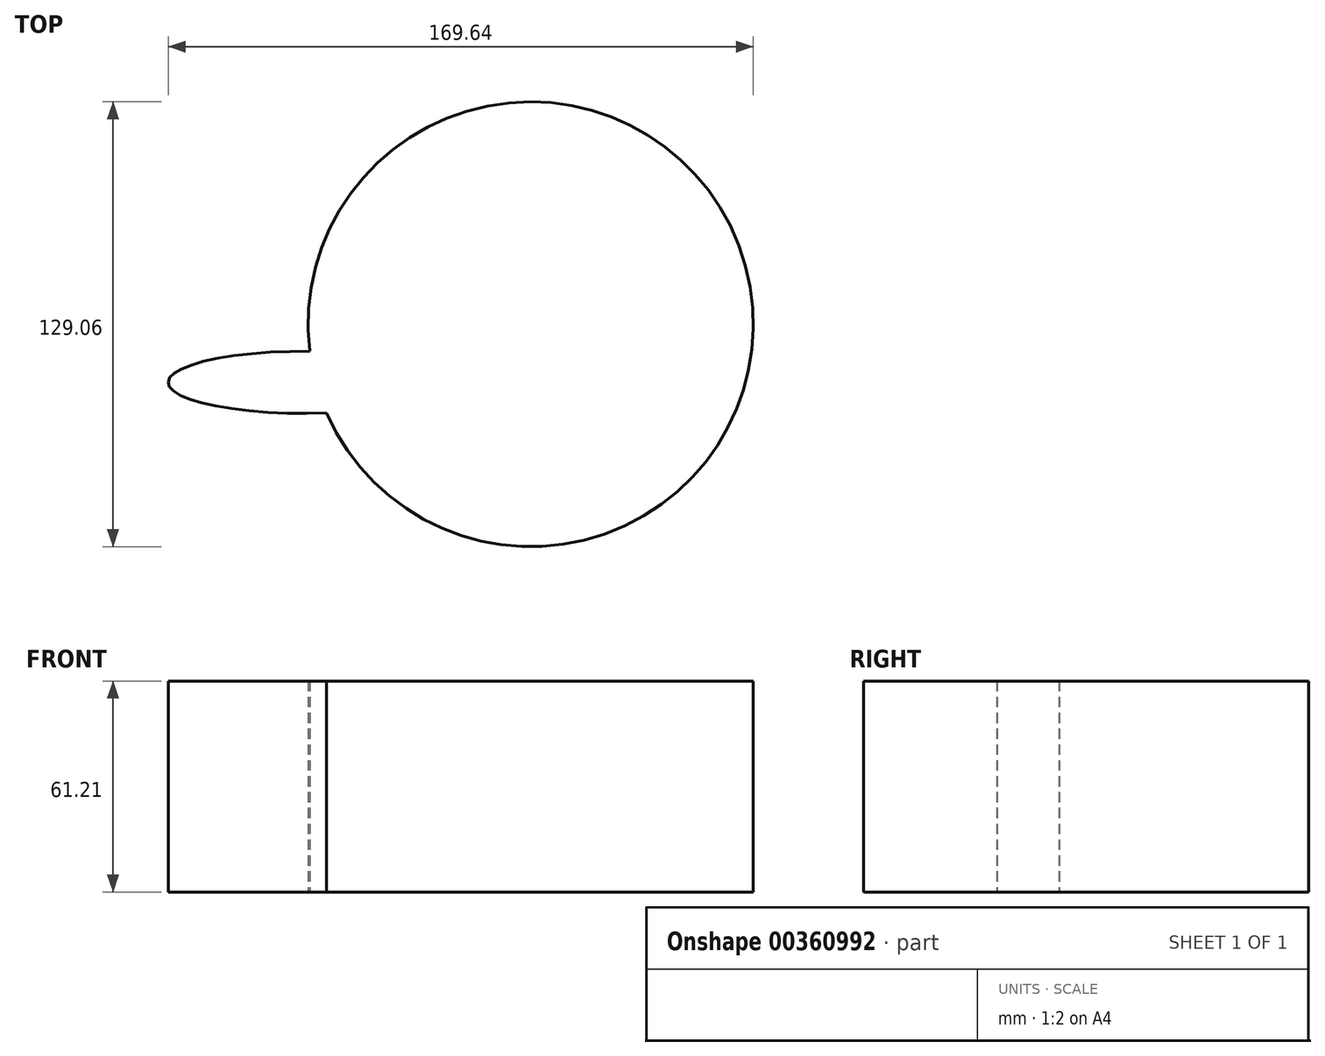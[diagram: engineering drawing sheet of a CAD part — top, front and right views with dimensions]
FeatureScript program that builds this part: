
annotation { "Feature Type Name" : "Feature", "Feature Type Description" : "" }
export const myFeature = defineFeature(function(context is Context, id is Id, definition is map)
    precondition{}
    {
        {
            var Q0;
            Q0=qCreatedBy(makeId("Top.planeOp"),FACE);
            var sketch = newSketch(context, id + "F0", { "sketchPlane" : qUnion([Q0])});
            skEllipse(sketch, "E0", {"center": v(-49.77, -16.17) * mm, "majorRadius": 39.4 * mm, "minorRadius": 9.03 * mm, "majorAxis": v(1, 0)});
            skCircle(sketch, "E1", {"center": v(15.94, 0.7) * mm, "radius": 64.53 * mm});
            skPoint(sketch, "E1.first.point", {"position": v(80.47, 0) * mm});
            skPoint(sketch, "E1.second.point", {"position": v(-43.6, 25.55) * mm});
            skPoint(sketch, "E1.third.point", {"position": v(0, 63.23) * mm});
            skSolve(sketch);
        }
        {
            var Q0;
            Q0 = qSketchRegion(id + "F0", true);
            extrude(context, id + "F1", {"entities" : qUnion([Q0]), "depth" : 61.2 * mm});
        }
    });
